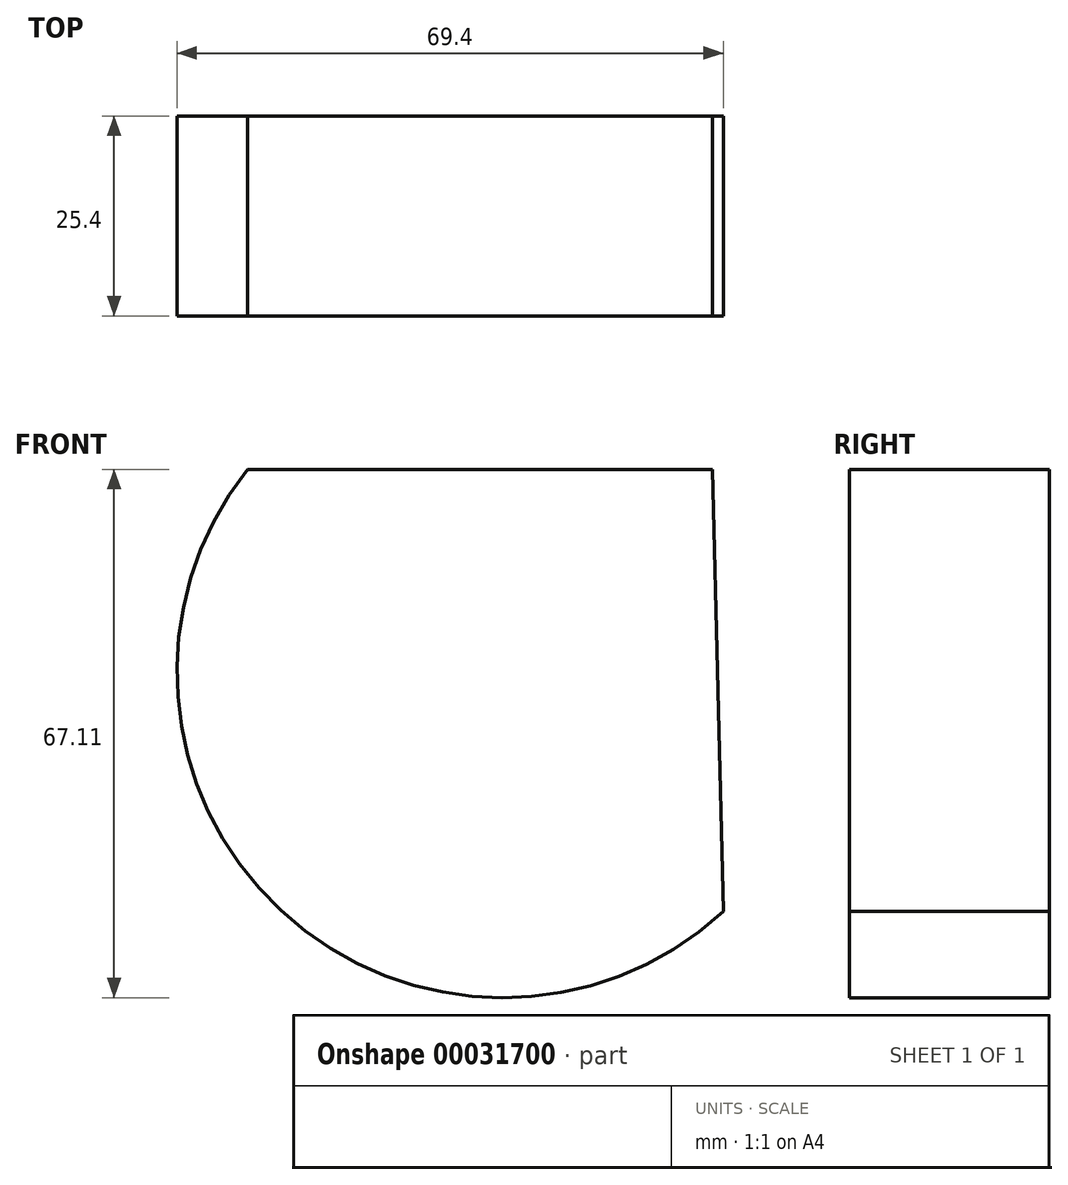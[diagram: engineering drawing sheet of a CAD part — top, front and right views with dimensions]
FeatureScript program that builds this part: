
annotation { "Feature Type Name" : "Feature", "Feature Type Description" : "" }
export const myFeature = defineFeature(function(context is Context, id is Id, definition is map)
    precondition{}
    {
        {
            var Q0;
            Q0=qCreatedBy(makeId("Front.planeOp"),FACE);
            var sketch = newSketch(context, id + "F0", { "sketchPlane" : qUnion([Q0])});
            skLineSegment(sketch, "E0", {"start": v(-33, 35.52) * mm, "end": v(26.07, 35.52) * mm});
            skLineSegment(sketch, "E1", {"start": v(26.07, 35.52) * mm, "end": v(27.44, -20.66) * mm});
            skArc(sketch, "E2", {"start": v(-33, 35.52) * mm, "mid": v(-28.76, -20.51) * mm, "end": v(27.44, -20.66) * mm});
            skSolve(sketch);
        }
        {
            var Q0;
            Q0 = qSketchRegion(id + "F0", true);
            extrude(context, id + "F1", {"entities" : qUnion([Q0]), "depth" : 25.4 * mm});
        }
    });
